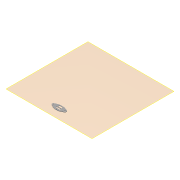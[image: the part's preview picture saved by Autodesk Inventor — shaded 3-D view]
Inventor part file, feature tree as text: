
AUTODESK INVENTOR PART (.ipt)
format: ipt  version: 2014 (Build 180170000, 170)  size: 170,496 bytes
history: native  units: mm
features: extrude x2, sketch x2, plane x1, fillet x1, reference x1
ambient origin geometry x8: Origin, YZ Plane, XZ Plane, XY Plane, X Axis, Y Axis, Z Axis, Center Point
bodies: Solid1 (feature_tree)
feature tree (7):
  plane  "Work Plane1"
  extrude  "Extrusion1"  Depth=30.0mm
  fillet  "Fillet1"  Radius=30.0mm
  extrude  "Extrusion2"  Depth=10.0mm
  sketch  "Sketch1"  dims[d2=14.0mm d3=14.0mm d5=30.0mm]
  reference  "Reference1"
  sketch  "Sketch2"  dims[d6=2.0mm d7=2.0mm d8=1.5mm d9=1.5mm d10=0.0mm d11=30.0mm d12=3.0mm d13=5.0mm d14=10.0mm d15=0.0mm d16=4.3mm d17=4.3mm]
